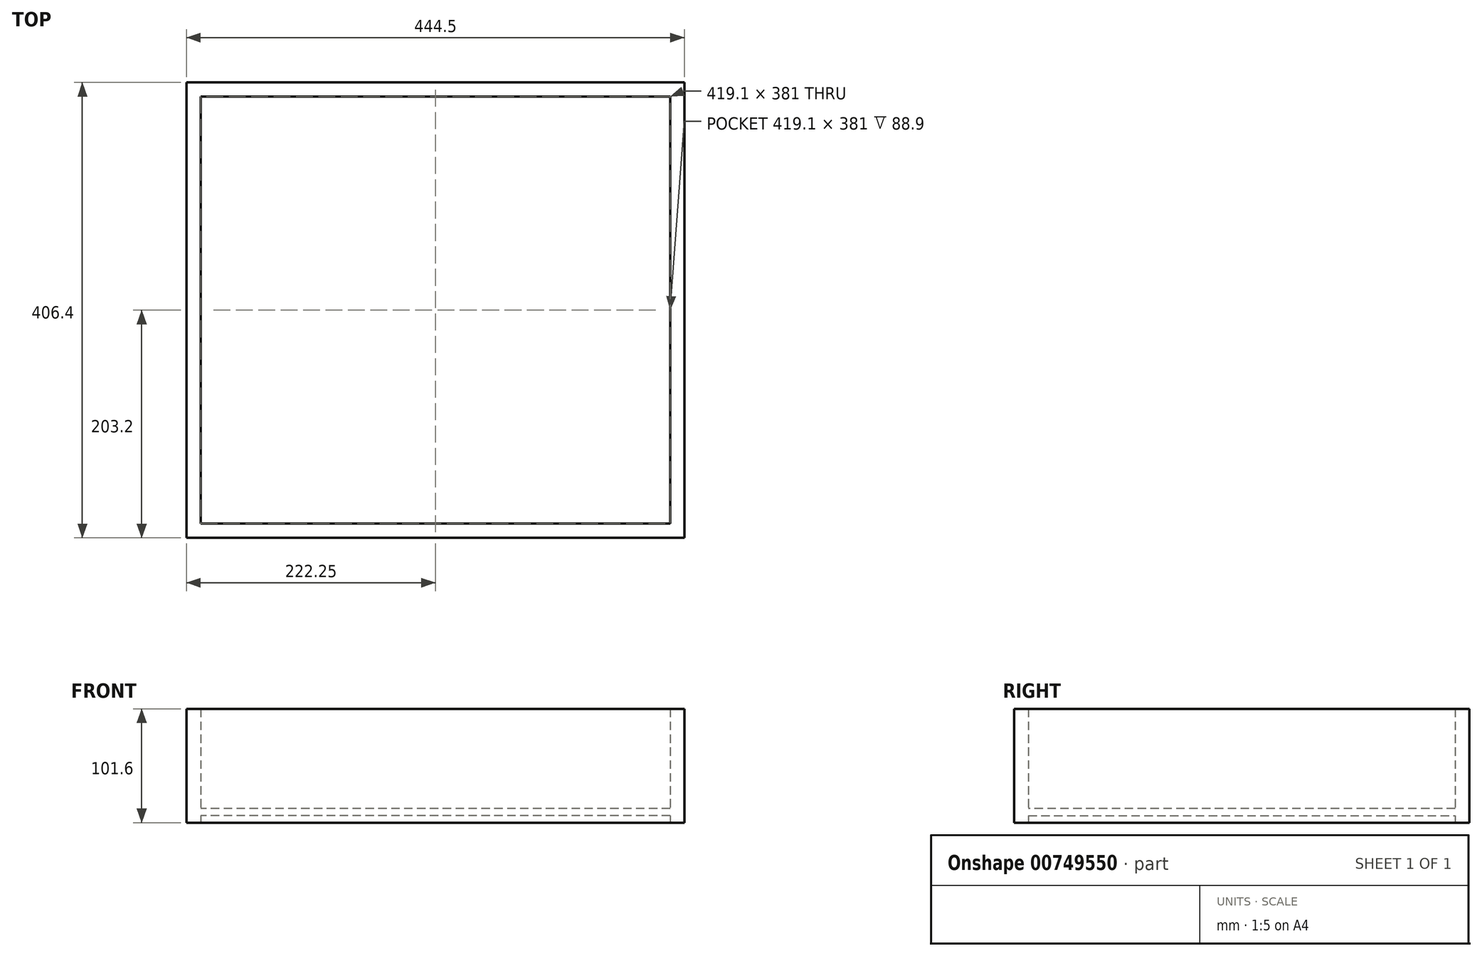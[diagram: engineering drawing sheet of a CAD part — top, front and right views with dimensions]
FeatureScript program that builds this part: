
annotation { "Feature Type Name" : "Feature", "Feature Type Description" : "" }
export const myFeature = defineFeature(function(context is Context, id is Id, definition is map)
    precondition{}
    {
        {
            var Q0;
            Q0=qCreatedBy(makeId("Top.planeOp"),FACE);
            var sketch = newSketch(context, id + "F0", { "sketchPlane" : qUnion([Q0])});
            skLineSegment(sketch, "E0.bottom", {"start": v(222.25, 203.2) * mm, "end": v(-222.25, 203.2) * mm});
            skLineSegment(sketch, "E0.top", {"start": v(222.25, -203.2) * mm, "end": v(-222.25, -203.2) * mm});
            skLineSegment(sketch, "E0.left", {"start": v(222.25, 203.2) * mm, "end": v(222.25, -203.2) * mm});
            skLineSegment(sketch, "E0.right", {"start": v(-222.25, 203.2) * mm, "end": v(-222.25, -203.2) * mm});
            skPoint(sketch, "E0.middle", {"position": v(0, 0) * mm});
            skLineSegment(sketch, "E1.bottom", {"start": v(209.55, 190.5) * mm, "end": v(-209.55, 190.5) * mm});
            skLineSegment(sketch, "E1.top", {"start": v(209.55, -190.5) * mm, "end": v(-209.55, -190.5) * mm});
            skLineSegment(sketch, "E1.left", {"start": v(209.55, 190.5) * mm, "end": v(209.55, -190.5) * mm});
            skLineSegment(sketch, "E1.right", {"start": v(-209.55, 190.5) * mm, "end": v(-209.55, -190.5) * mm});
            skSolve(sketch);
        }
        {
            var Q0;
            Q0=makeQuery(id+"F0.imprint","IMPRINT",FACE,{"disambiguationData":[TD([[makeQuery(id+"F0.imprint","IMPRINT",EDGE,{"derivedFrom":sQuery(id+"F0.wireOp",EDGE,"E0.bottom")}),1.0]])]});
            extrude(context, id + "F1", {"entities" : qUnion([Q0]), "depth" : 63.5 * mm, "offsetDistance" : 25.4 * mm});
        }
        {
            var Q0;
            Q0=makeQuery(id+"F1.opExtrude","CAP_FACE",FACE,{"disambiguationData":[OSD([sQuery(id+"F0.wireOp",EDGE,"E0.bottom"),sQuery(id+"F0.wireOp",EDGE,"E0.top"),sQuery(id+"F0.wireOp",EDGE,"E0.left"),sQuery(id+"F0.wireOp",EDGE,"E0.right"),sQuery(id+"F0.wireOp",EDGE,"E1.bottom"),sQuery(id+"F0.wireOp",EDGE,"E1.top"),sQuery(id+"F0.wireOp",EDGE,"E1.left"),sQuery(id+"F0.wireOp",EDGE,"E1.right")])],"isStart":true});
            var sketch = newSketch(context, id + "F2", { "sketchPlane" : qUnion([Q0])});
            skLineSegment(sketch, "E2.bottom", {"start": v(-209.55, 190.5) * mm, "end": v(209.55, 190.5) * mm});
            skLineSegment(sketch, "E2.top", {"start": v(-209.55, -190.5) * mm, "end": v(209.55, -190.5) * mm});
            skLineSegment(sketch, "E2.left", {"start": v(-209.55, 190.5) * mm, "end": v(-209.55, -190.5) * mm});
            skLineSegment(sketch, "E2.right", {"start": v(209.55, 190.5) * mm, "end": v(209.55, -190.5) * mm});
            skPoint(sketch, "E2.middle", {"position": v(0, 0) * mm});
            skSolve(sketch);
        }
        {
            var Q0;
            Q0=makeQuery(id+"F2.imprint","IMPRINT",FACE,{"disambiguationData":[TD([[makeQuery(id+"F2.imprint","IMPRINT",EDGE,{"derivedFrom":sQuery(id+"F2.wireOp",EDGE,"E2.bottom")}),1.0]])]});
            extrude(context, id + "F3", {"entities" : qUnion([Q0]), "operationType" : NewBodyOperationType.ADD, "oppositeDirection" : true, "depth" : 12.7 * mm, "offsetDistance" : 25.4 * mm});
        }
        {
            var Q0;
            Q0=makeQuery(id+"F3.boolean.opBoolean","MERGE",FACE,{"derivedFrom":[makeQuery(id+"F1.opExtrude","CAP_FACE",FACE,{"disambiguationData":[OSD([sQuery(id+"F0.wireOp",EDGE,"E0.bottom"),sQuery(id+"F0.wireOp",EDGE,"E0.top"),sQuery(id+"F0.wireOp",EDGE,"E0.left"),sQuery(id+"F0.wireOp",EDGE,"E0.right"),sQuery(id+"F0.wireOp",EDGE,"E1.bottom"),sQuery(id+"F0.wireOp",EDGE,"E1.top"),sQuery(id+"F0.wireOp",EDGE,"E1.left"),sQuery(id+"F0.wireOp",EDGE,"E1.right")])],"isStart":true}),makeQuery(id+"F3.opExtrude","CAP_FACE",FACE,{"disambiguationData":[OSD([sQuery(id+"F2.wireOp",EDGE,"E2.bottom"),sQuery(id+"F2.wireOp",EDGE,"E2.top"),sQuery(id+"F2.wireOp",EDGE,"E2.left"),sQuery(id+"F2.wireOp",EDGE,"E2.right")])],"isStart":true})]});
            var sketch = newSketch(context, id + "F4", { "sketchPlane" : qUnion([Q0])});
            skLineSegment(sketch, "E3.bottom", {"start": v(209.55, 190.5) * mm, "end": v(-209.55, 190.5) * mm});
            skLineSegment(sketch, "E3.top", {"start": v(209.55, -190.5) * mm, "end": v(-209.55, -190.5) * mm});
            skLineSegment(sketch, "E3.left", {"start": v(209.55, 190.5) * mm, "end": v(209.55, -190.5) * mm});
            skLineSegment(sketch, "E3.right", {"start": v(-209.55, 190.5) * mm, "end": v(-209.55, -190.5) * mm});
            skPoint(sketch, "E3.middle", {"position": v(0, 0) * mm});
            skSolve(sketch);
        }
        {
            var Q0;
            Q0=makeQuery(id+"F4.imprint","IMPRINT",FACE,{"disambiguationData":[TD([[makeQuery(id+"F4.imprint","IMPRINT",EDGE,{"derivedFrom":sQuery(id+"F4.wireOp",EDGE,"E3.bottom")}),1.0]])]});
            extrude(context, id + "F5", {"entities" : qUnion([Q0]), "operationType" : NewBodyOperationType.REMOVE, "oppositeDirection" : true, "depth" : 6.35 * mm, "offsetDistance" : 25.4 * mm});
        }
        {
            var Q0;
            Q0=makeQuery(id+"F1.opExtrude","CAP_FACE",FACE,{"disambiguationData":[OSD([sQuery(id+"F0.wireOp",EDGE,"E0.bottom"),sQuery(id+"F0.wireOp",EDGE,"E0.top"),sQuery(id+"F0.wireOp",EDGE,"E0.left"),sQuery(id+"F0.wireOp",EDGE,"E0.right"),sQuery(id+"F0.wireOp",EDGE,"E1.bottom"),sQuery(id+"F0.wireOp",EDGE,"E1.top"),sQuery(id+"F0.wireOp",EDGE,"E1.left"),sQuery(id+"F0.wireOp",EDGE,"E1.right")])],"isStart":false});
            extrude(context, id + "F6", {"entities" : qUnion([Q0]), "operationType" : NewBodyOperationType.ADD, "depth" : 38.1 * mm, "offsetDistance" : 25.4 * mm});
        }
    });
